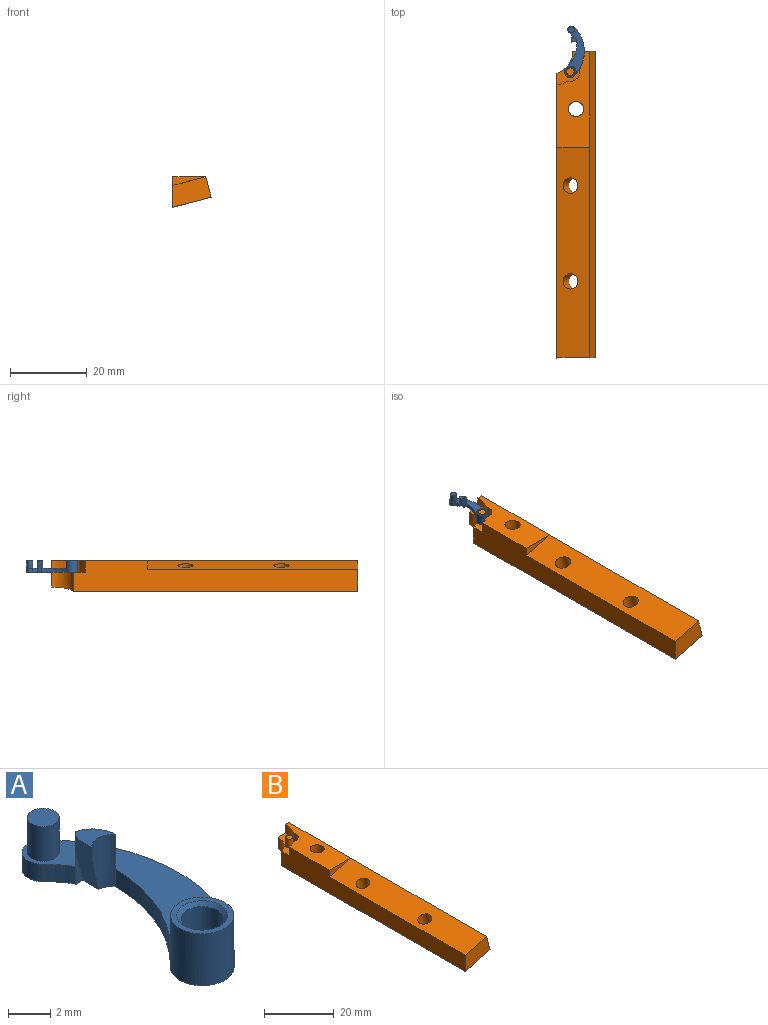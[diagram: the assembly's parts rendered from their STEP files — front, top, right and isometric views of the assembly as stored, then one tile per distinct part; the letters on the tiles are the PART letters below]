
ASSEMBLY  parts=2 mates=1
PART A: 19 faces, bbox 5.5x13.8x3.3 mm
  f0: plane 1.55x1.5mm, normal (0,0,1), area 1.3mm2, adj f1,f2,f12,f17
  f1: cylinder r=1.53mm len=3mm, axis (0,0,-1), area 0.6mm2, adj f0,f3,f6,f12,f17,f18
  f2: cylinder r=1.01mm len=3mm, axis (0,0,-1), area 3.9mm2, adj f0,f3,f7,f12,f17
  f3: plane 13.46x5.2mm, normal (0,0,-1), area 29mm2, adj f1,f2,f4,f5,f6,f7,f10,f15
  f4: cylinder r=9mm len=12.73mm, axis (0,0,-1), area 14.1mm2, adj f3,f5,f10,f11
  f5: cylinder r=1mm len=1.71mm, axis (0,0,-1), area 3.1mm2, adj f3,f4,f6,f11
  f6: cylinder r=7mm len=1.19mm, axis (0,0,-1), area 1.5mm2, adj f1,f3,f5,f11
  f7: cylinder r=9.16mm len=6.51mm, axis (0,0,-1), area 7.4mm2, adj f2,f3,f8,f10,f11
  f8: plane 3x3mm, normal (0,0,1), area 2.5mm2, adj f7,f10,f16
  f9: cylinder r=1mm len=2.6mm, axis (0,0,-1), area 16.3mm2, adj f15,f16
  f10: cylinder r=1.5mm len=3mm, axis (0,0,-1), area 23.4mm2, adj f3,f4,f7,f8,f11
  f11: plane 13.02x4.71mm, normal (0,0,1), area 24.2mm2, adj f4,f5,f6,f7,f10,f12,f13
  f12: cylinder r=1.54mm len=2mm, axis (0,0,1), area 4.1mm2, adj f0,f1,f2,f11
  f13: cylinder r=0.75mm len=2mm, axis (0,0,-1), area 9.4mm2, adj f11,f14
  f14: plane 1.5x1.5mm, normal (0,0,1), area 1.8mm2, adj f13
  f15: cone r=1.2mm half-angle=45deg, axis (0,0,-1), area 2mm2, adj f3,f9
  f16: cone r=1mm half-angle=45deg, axis (0,0,1), area 2mm2, adj f8,f9
  f17: plane 3.3x1.69mm, normal (-0.97,0,-0.26), area 3.3mm2, adj f0,f1,f2,f3,f18
  f18: plane 1.92x0.51mm, normal (0,-1,0), area 0.5mm2, adj f1,f3,f17
PART B: 18 faces, bbox 10x80x8 mm
  f0: plane 25x8.57mm, normal (0,0,1), area 151.1mm2, adj f1,f4,f6,f7,f8,f13,f15,f17
  f1: plane 74.28x8mm, normal (-1,0,0), area 458.6mm2, adj f0,f5,f7,f9,f10,f14,f16,f17
  f2: cylinder r=2mm len=6.36mm, axis (0.26,0,-0.97), area 69.2mm2, adj f14,f16
  f3: cylinder r=2mm len=6.36mm, axis (0.26,0,-0.97), area 69.2mm2, adj f14,f16
  f4: plane 6.87x5.8mm, normal (0,1,0), area 22.6mm2, adj f0,f5,f8,f10,f14,f15
  f5: cylinder r=6mm len=5.72mm, axis (0,0,1), area 32.4mm2, adj f1,f4,f10,f14
  f6: cylinder r=2mm len=7.2mm, axis (0,0,1), area 83.7mm2, adj f0,f14
  f7: cylinder r=9mm len=3mm, axis (0,0,-1), area 9.2mm2, adj f0,f1,f10,f13
  f8: cylinder r=9mm len=4.64mm, axis (0,0,-1), area 14.6mm2, adj f0,f4,f10,f13
  f9: plane 10x8mm, normal (0,-1,0), area 53mm2, adj f1,f14,f15,f16
  f10: plane 8.82x7.2mm, normal (0,0,1), area 29.9mm2, adj f1,f4,f5,f7,f8,f11,f13
  f11: cylinder r=1mm len=3mm, axis (0,0,-1), area 18.8mm2, adj f10,f12
  f12: plane 2x2mm, normal (0,0,1), area 3.1mm2, adj f11
  f13: cylinder r=2.5mm len=3.17mm, axis (0,0,1), area 15.8mm2, adj f0,f7,f8,f10
  f14: plane 80x10mm, normal (0.26,0,-0.97), area 771.8mm2, adj f1,f2,f3,f4,f5,f6,f9,f15
  f15: plane 80x5.32mm, normal (0.97,0,0.26), area 440.7mm2, adj f0,f4,f9,f14,f16
  f16: plane 55x8.57mm, normal (-0.26,0,0.97), area 463.1mm2, adj f1,f2,f3,f9,f15,f17
  f17: plane 8.57x2.3mm, normal (0,-1,0), area 9.8mm2, adj f0,f1,f16
PLACE A t=(-6.5,2.2,0)mm
PLACE B at identity
MATE cylindrical A.f9 <-> B.f11  axis (0,0,1) through (-6.5,-5.3,3)mm
